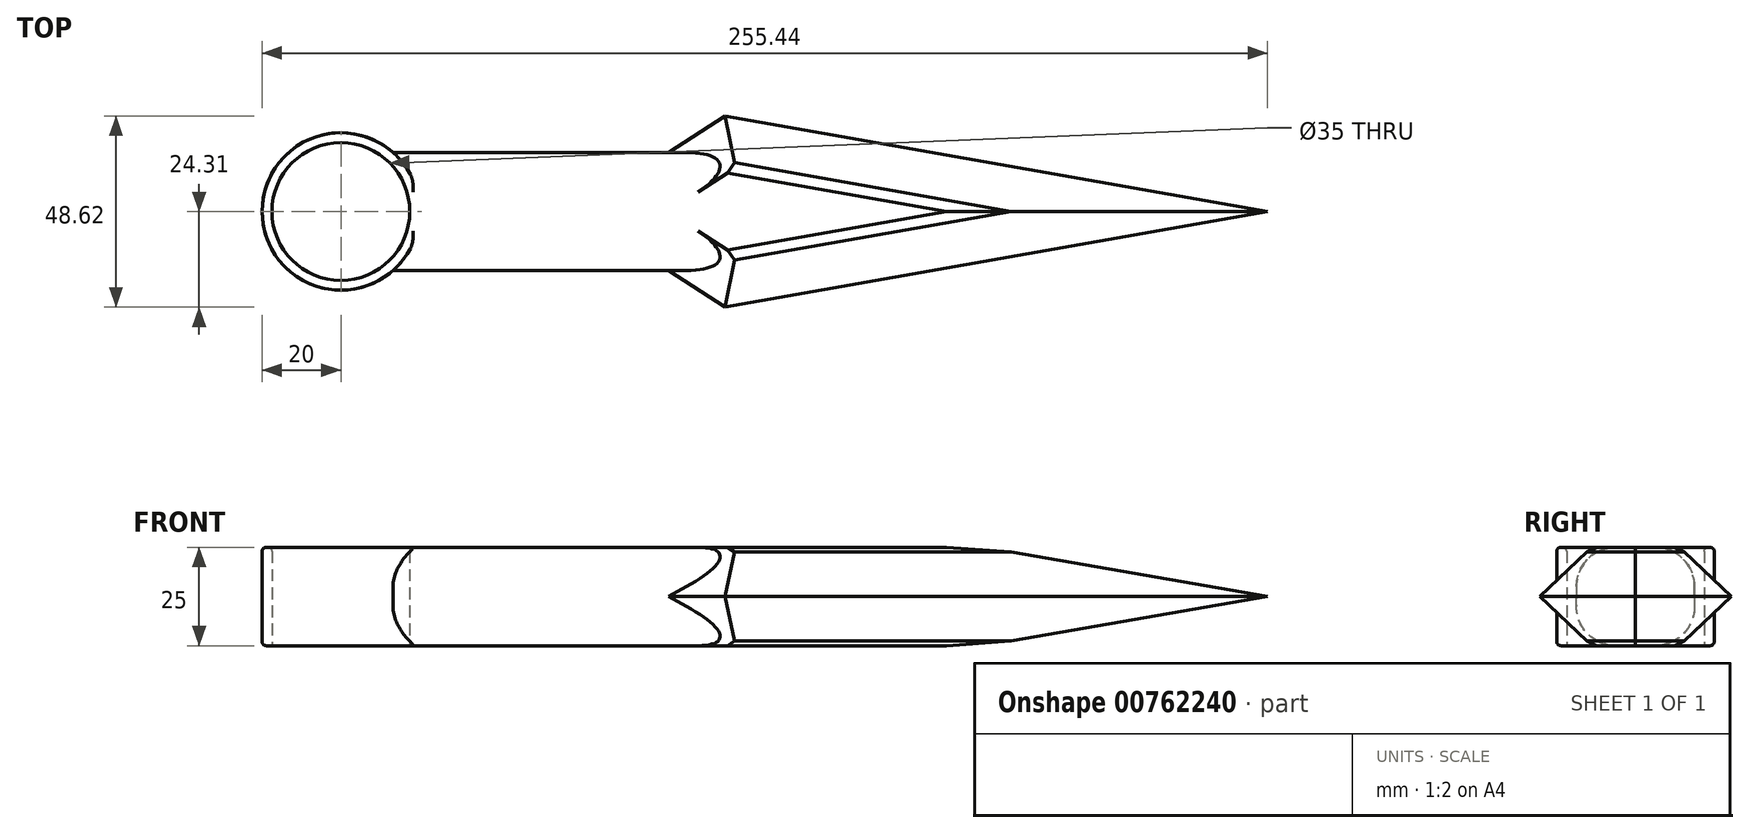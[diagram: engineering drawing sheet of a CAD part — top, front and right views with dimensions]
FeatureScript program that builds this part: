
annotation { "Feature Type Name" : "Feature", "Feature Type Description" : "" }
export const myFeature = defineFeature(function(context is Context, id is Id, definition is map)
    precondition{}
    {
        {
            var Q0;
            Q0=qCreatedBy(makeId("Top.planeOp"),FACE);
            var sketch = newSketch(context, id + "F0", { "sketchPlane" : qUnion([Q0])});
            skCircle(sketch, "E0", {"center": v(0, 0) * mm, "radius": 20 * mm});
            skCircle(sketch, "E1", {"center": v(0, 0) * mm, "radius": 17.5 * mm});
            skPoint(sketch, "E2", {"position": v(13.23, 15) * mm});
            skPoint(sketch, "E3", {"position": v(13.23, -15) * mm});
            skLineSegment(sketch, "E4.bottom", {"start": v(13.23, 15) * mm, "end": v(83.23, 15) * mm});
            skLineSegment(sketch, "E4.top", {"start": v(13.23, -15) * mm, "end": v(83.23, -15) * mm});
            skLineSegment(sketch, "E4.left", {"start": v(13.23, 15) * mm, "end": v(13.23, -15) * mm});
            skLineSegment(sketch, "E4.right", {"start": v(83.23, 15) * mm, "end": v(83.23, -15) * mm});
            skSolve(sketch);
        }
        {
            var Q0;
            Q0=makeQuery(id+"F0.imprint","IMPRINT",FACE,{"disambiguationData":[TD([[makeQuery(id+"F0.imprint","IMPRINT",EDGE,{"derivedFrom":sQuery(id+"F0.wireOp",EDGE,"E0")}),1.0]])]});
            var Q1;
            {var subQ1=sQuery(id+"F0.wireOp",EDGE,"E4.bottom");Q1=makeQuery(id+"F0.imprint","IMPRINT",FACE,{"disambiguationData":[TD([[makeQuery(id+"F0.imprint","IMPRINT",EDGE,{"derivedFrom":subQ1}),-1.0]])]});}
            extrude(context, id + "F1", {"entities" : qUnion([Q0, Q1]), "endBound" : BoundingType.SYMMETRIC, "depth" : 25 * mm, "offsetDistance" : 25 * mm});
        }
        {
            var Q0;
            Q0=qCreatedBy(makeId("Top.planeOp"),FACE);
            var sketch = newSketch(context, id + "F2", { "sketchPlane" : qUnion([Q0])});
            skLineSegment(sketch, "E5", {"start": v(83.23, 15) * mm, "end": v(97.57, 24.31) * mm});
            skLineSegment(sketch, "E6", {"start": v(97.57, 24.31) * mm, "end": v(235.44, 0) * mm});
            skLineSegment(sketch, "E7", {"start": v(235.44, 0) * mm, "end": v(97.57, -24.31) * mm});
            skLineSegment(sketch, "E8", {"start": v(97.57, -24.31) * mm, "end": v(83.23, -15) * mm});
            skLineSegment(sketch, "E9", {"start": v(83.23, 15) * mm, "end": v(83.23, -15) * mm});
            skSolve(sketch);
        }
        {
            var Q0;
            Q0 = qSketchRegion(id + "F2", true);
            extrude(context, id + "F3", {"entities" : qUnion([Q0]), "operationType" : NewBodyOperationType.ADD, "endBound" : BoundingType.SYMMETRIC, "depth" : 25 * mm, "offsetDistance" : 25 * mm});
        }
        {
            var Q0;
            Q0=makeQuery(id+"F1.opExtrude","CAP_EDGE",EDGE,{"disambiguationData":[OSD([sQuery(id+"F0.wireOp",EDGE,"E4.top")])],"isStart":false});
            var Q1;
            Q1=makeQuery(id+"F1.opExtrude","CAP_EDGE",EDGE,{"disambiguationData":[OSD([sQuery(id+"F0.wireOp",EDGE,"E4.bottom")])],"isStart":false});
            var Q2;
            Q2=makeQuery(id+"F1.opExtrude","CAP_EDGE",EDGE,{"disambiguationData":[OSD([sQuery(id+"F0.wireOp",EDGE,"E4.top")])],"isStart":true});
            var Q3;
            Q3=makeQuery(id+"F1.opExtrude","CAP_EDGE",EDGE,{"disambiguationData":[OSD([sQuery(id+"F0.wireOp",EDGE,"E4.bottom")])],"isStart":true});
            fillet(context, id + "F4", {"entities" : qUnion([Q0, Q1, Q2, Q3]), "radius" : 10 * mm, "tangentPropagation" : true, "allowEdgeOverflow" : false});
        }
        {
            var Q0;
            Q0=makeQuery(id+"F3.opExtrude","CAP_EDGE",EDGE,{"disambiguationData":[OSD([sQuery(id+"F2.wireOp",EDGE,"E7")])],"isStart":false});
            var Q1;
            Q1=makeQuery(id+"F3.opExtrude","CAP_EDGE",EDGE,{"disambiguationData":[OSD([sQuery(id+"F2.wireOp",EDGE,"E8")])],"isStart":false});
            var Q2;
            Q2=makeQuery(id+"F3.opExtrude","CAP_EDGE",EDGE,{"disambiguationData":[OSD([sQuery(id+"F2.wireOp",EDGE,"E8")])],"isStart":true});
            var Q3;
            Q3=makeQuery(id+"F3.opExtrude","CAP_EDGE",EDGE,{"disambiguationData":[OSD([sQuery(id+"F2.wireOp",EDGE,"E7")])],"isStart":true});
            var Q4;
            Q4=makeQuery(id+"F3.opExtrude","CAP_EDGE",EDGE,{"disambiguationData":[OSD([sQuery(id+"F2.wireOp",EDGE,"E5")])],"isStart":false});
            var Q5;
            Q5=makeQuery(id+"F3.opExtrude","CAP_EDGE",EDGE,{"disambiguationData":[OSD([sQuery(id+"F2.wireOp",EDGE,"E6")])],"isStart":false});
            var Q6;
            Q6=makeQuery(id+"F3.opExtrude","CAP_EDGE",EDGE,{"disambiguationData":[OSD([sQuery(id+"F2.wireOp",EDGE,"E5")])],"isStart":true});
            var Q7;
            Q7=makeQuery(id+"F3.opExtrude","CAP_EDGE",EDGE,{"disambiguationData":[OSD([sQuery(id+"F2.wireOp",EDGE,"E6")])],"isStart":true});
            chamfer(context, id + "F5", {"entities" : qUnion([Q0, Q1, Q2, Q3, Q4, Q5, Q6, Q7]), "width" : 12.5 * mm, "tangentPropagation" : true});
        }
        {
            var Q0;
            Q0=makeQuery(id+"F1.opExtrude","CAP_EDGE",EDGE,{"disambiguationData":[OSD([sQuery(id+"F0.wireOp",EDGE,"E0")])],"isStart":true});
            var Q1;
            Q1=makeQuery(id+"F1.opExtrude","CAP_EDGE",EDGE,{"disambiguationData":[OSD([sQuery(id+"F0.wireOp",EDGE,"E0")])],"isStart":false});
            fillet(context, id + "F6", {"entities" : qUnion([Q0, Q1]), "radius" : 1 * mm, "tangentPropagation" : true, "allowEdgeOverflow" : false});
        }
        {
            var Q0;
            Q0=makeQuery(id+"F1.opExtrude","CAP_EDGE",EDGE,{"disambiguationData":[OSD([sQuery(id+"F0.wireOp",EDGE,"E1")])],"isStart":false});
            fillet(context, id + "F7", {"entities" : qUnion([Q0]), "radius" : 1 * mm, "tangentPropagation" : true, "allowEdgeOverflow" : false});
        }
        {
            var Q0;
            {var subQ0=sQuery(id+"F2.wireOp",EDGE,"E6");Q0=makeQuery(id+"F5.opChamfer","BLEND_EDGE",EDGE,{"blendedFrom":[makeQuery(id+"F3.opExtrude","CAP_EDGE",EDGE,{"disambiguationData":[OSD([subQ0])],"isStart":true}),makeQuery(id+"F3.boolean.opBoolean","MERGE",FACE,{"derivedFrom":[makeQuery(id+"F1.opExtrude","CAP_FACE",FACE,{"disambiguationData":[OSD([sQuery(id+"F0.wireOp",EDGE,"E0"),sQuery(id+"F0.wireOp",EDGE,"E1"),sQuery(id+"F0.wireOp",EDGE,"E4.bottom"),sQuery(id+"F0.wireOp",EDGE,"E4.top"),sQuery(id+"F0.wireOp",EDGE,"E4.right")])],"isStart":true}),makeQuery(id+"F3.opExtrude","CAP_FACE",FACE,{"disambiguationData":[OSD([sQuery(id+"F2.wireOp",EDGE,"E5"),subQ0,sQuery(id+"F2.wireOp",EDGE,"E7"),sQuery(id+"F2.wireOp",EDGE,"E8"),sQuery(id+"F2.wireOp",EDGE,"E9")])],"isStart":true})]})],"blendedInto":[makeQuery(id+"F3.boolean.opBoolean","MERGE",FACE,{"derivedFrom":[makeQuery(id+"F1.opExtrude","CAP_FACE",FACE,{"disambiguationData":[OSD([sQuery(id+"F0.wireOp",EDGE,"E0"),sQuery(id+"F0.wireOp",EDGE,"E1"),sQuery(id+"F0.wireOp",EDGE,"E4.bottom"),sQuery(id+"F0.wireOp",EDGE,"E4.top"),sQuery(id+"F0.wireOp",EDGE,"E4.right")])],"isStart":true}),makeQuery(id+"F3.opExtrude","CAP_FACE",FACE,{"disambiguationData":[OSD([sQuery(id+"F2.wireOp",EDGE,"E5"),subQ0,sQuery(id+"F2.wireOp",EDGE,"E7"),sQuery(id+"F2.wireOp",EDGE,"E8"),sQuery(id+"F2.wireOp",EDGE,"E9")])],"isStart":true})]})]});}
            var Q1;
            {var subQ0=sQuery(id+"F2.wireOp",EDGE,"E7");Q1=makeQuery(id+"F5.opChamfer","BLEND_EDGE",EDGE,{"blendedFrom":[makeQuery(id+"F3.opExtrude","CAP_EDGE",EDGE,{"disambiguationData":[OSD([subQ0])],"isStart":true}),makeQuery(id+"F3.boolean.opBoolean","MERGE",FACE,{"derivedFrom":[makeQuery(id+"F1.opExtrude","CAP_FACE",FACE,{"disambiguationData":[OSD([sQuery(id+"F0.wireOp",EDGE,"E0"),sQuery(id+"F0.wireOp",EDGE,"E1"),sQuery(id+"F0.wireOp",EDGE,"E4.bottom"),sQuery(id+"F0.wireOp",EDGE,"E4.top"),sQuery(id+"F0.wireOp",EDGE,"E4.right")])],"isStart":true}),makeQuery(id+"F3.opExtrude","CAP_FACE",FACE,{"disambiguationData":[OSD([sQuery(id+"F2.wireOp",EDGE,"E5"),sQuery(id+"F2.wireOp",EDGE,"E6"),subQ0,sQuery(id+"F2.wireOp",EDGE,"E8"),sQuery(id+"F2.wireOp",EDGE,"E9")])],"isStart":true})]})],"blendedInto":[makeQuery(id+"F3.boolean.opBoolean","MERGE",FACE,{"derivedFrom":[makeQuery(id+"F1.opExtrude","CAP_FACE",FACE,{"disambiguationData":[OSD([sQuery(id+"F0.wireOp",EDGE,"E0"),sQuery(id+"F0.wireOp",EDGE,"E1"),sQuery(id+"F0.wireOp",EDGE,"E4.bottom"),sQuery(id+"F0.wireOp",EDGE,"E4.top"),sQuery(id+"F0.wireOp",EDGE,"E4.right")])],"isStart":true}),makeQuery(id+"F3.opExtrude","CAP_FACE",FACE,{"disambiguationData":[OSD([sQuery(id+"F2.wireOp",EDGE,"E5"),sQuery(id+"F2.wireOp",EDGE,"E6"),subQ0,sQuery(id+"F2.wireOp",EDGE,"E8"),sQuery(id+"F2.wireOp",EDGE,"E9")])],"isStart":true})]})]});}
            var Q2;
            {var subQ0=sQuery(id+"F2.wireOp",EDGE,"E6");Q2=makeQuery(id+"F5.opChamfer","BLEND_EDGE",EDGE,{"blendedFrom":[makeQuery(id+"F3.opExtrude","CAP_EDGE",EDGE,{"disambiguationData":[OSD([subQ0])],"isStart":false}),makeQuery(id+"F3.boolean.opBoolean","MERGE",FACE,{"derivedFrom":[makeQuery(id+"F1.opExtrude","CAP_FACE",FACE,{"disambiguationData":[OSD([sQuery(id+"F0.wireOp",EDGE,"E0"),sQuery(id+"F0.wireOp",EDGE,"E1"),sQuery(id+"F0.wireOp",EDGE,"E4.bottom"),sQuery(id+"F0.wireOp",EDGE,"E4.top"),sQuery(id+"F0.wireOp",EDGE,"E4.right")])],"isStart":false}),makeQuery(id+"F3.opExtrude","CAP_FACE",FACE,{"disambiguationData":[OSD([sQuery(id+"F2.wireOp",EDGE,"E5"),subQ0,sQuery(id+"F2.wireOp",EDGE,"E7"),sQuery(id+"F2.wireOp",EDGE,"E8"),sQuery(id+"F2.wireOp",EDGE,"E9")])],"isStart":false})]})],"blendedInto":[makeQuery(id+"F3.boolean.opBoolean","MERGE",FACE,{"derivedFrom":[makeQuery(id+"F1.opExtrude","CAP_FACE",FACE,{"disambiguationData":[OSD([sQuery(id+"F0.wireOp",EDGE,"E0"),sQuery(id+"F0.wireOp",EDGE,"E1"),sQuery(id+"F0.wireOp",EDGE,"E4.bottom"),sQuery(id+"F0.wireOp",EDGE,"E4.top"),sQuery(id+"F0.wireOp",EDGE,"E4.right")])],"isStart":false}),makeQuery(id+"F3.opExtrude","CAP_FACE",FACE,{"disambiguationData":[OSD([sQuery(id+"F2.wireOp",EDGE,"E5"),subQ0,sQuery(id+"F2.wireOp",EDGE,"E7"),sQuery(id+"F2.wireOp",EDGE,"E8"),sQuery(id+"F2.wireOp",EDGE,"E9")])],"isStart":false})]})]});}
            var Q3;
            {var subQ0=sQuery(id+"F2.wireOp",EDGE,"E7");Q3=makeQuery(id+"F5.opChamfer","BLEND_EDGE",EDGE,{"blendedFrom":[makeQuery(id+"F3.opExtrude","CAP_EDGE",EDGE,{"disambiguationData":[OSD([subQ0])],"isStart":false}),makeQuery(id+"F3.boolean.opBoolean","MERGE",FACE,{"derivedFrom":[makeQuery(id+"F1.opExtrude","CAP_FACE",FACE,{"disambiguationData":[OSD([sQuery(id+"F0.wireOp",EDGE,"E0"),sQuery(id+"F0.wireOp",EDGE,"E1"),sQuery(id+"F0.wireOp",EDGE,"E4.bottom"),sQuery(id+"F0.wireOp",EDGE,"E4.top"),sQuery(id+"F0.wireOp",EDGE,"E4.right")])],"isStart":false}),makeQuery(id+"F3.opExtrude","CAP_FACE",FACE,{"disambiguationData":[OSD([sQuery(id+"F2.wireOp",EDGE,"E5"),sQuery(id+"F2.wireOp",EDGE,"E6"),subQ0,sQuery(id+"F2.wireOp",EDGE,"E8"),sQuery(id+"F2.wireOp",EDGE,"E9")])],"isStart":false})]})],"blendedInto":[makeQuery(id+"F3.boolean.opBoolean","MERGE",FACE,{"derivedFrom":[makeQuery(id+"F1.opExtrude","CAP_FACE",FACE,{"disambiguationData":[OSD([sQuery(id+"F0.wireOp",EDGE,"E0"),sQuery(id+"F0.wireOp",EDGE,"E1"),sQuery(id+"F0.wireOp",EDGE,"E4.bottom"),sQuery(id+"F0.wireOp",EDGE,"E4.top"),sQuery(id+"F0.wireOp",EDGE,"E4.right")])],"isStart":false}),makeQuery(id+"F3.opExtrude","CAP_FACE",FACE,{"disambiguationData":[OSD([sQuery(id+"F2.wireOp",EDGE,"E5"),sQuery(id+"F2.wireOp",EDGE,"E6"),subQ0,sQuery(id+"F2.wireOp",EDGE,"E8"),sQuery(id+"F2.wireOp",EDGE,"E9")])],"isStart":false})]})]});}
            chamfer(context, id + "F8", {"entities" : qUnion([Q0, Q1, Q2, Q3]), "width" : (4) * mm, "tangentPropagation" : true});
        }
    });
